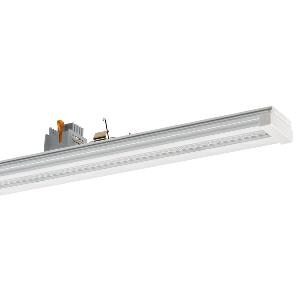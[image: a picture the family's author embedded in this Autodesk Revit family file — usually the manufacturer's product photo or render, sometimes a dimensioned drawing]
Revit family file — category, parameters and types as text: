
# Revit family: conveo_-_cvg_8000_850_xn-l_da_7_226848409-00804979_7b88
name_source: partatom
category: Lighting Fixtures
units: mm (PartAtom-declared; Revit-internal decimal feet)

## family parameters
Cut with Voids When Loaded = No
Host = Face
Light Source = No
Part Type = Normal
Room Calculation Point = No
Round Connector Dimension = Use Diameter
Shared = No

## types (1)
- CONVEO - CVG 8000/850/xN-L/DA/7 (1 x LED, 8450 lm, 5000K)
    Apparent Load = 51 VA
    Approval mark = CE
    CIE Flux Codes = 84 95 99 100 100
    Color Rendering = 80-89
    Color Temperature = 5000K
    Control Gear = Electronic ballast
    Default Elevation = 1800 mm
    Description = CVG 8000/850/xN-L/DA/7|Continuous-row system|light source: LED|work equipment: Adjustable electronic ballast, digital DALI|connected load: 220-240 V, 50-60 Hz|Power consumption: approx. 51 W|luminous flux: 8450 lm|luminous efficacy: 165 lm/W|colour temperature: Cold white, ca. 5000 K|color rendering index (CRI): >= 80|chromaticity tolerance:  3 SDCM|System of protection: IP 54|class of protection: I|technology: Continuously dimmable|luminaire body|material: Aluminium|surface: Powder coatet|colour: White|lamp cover: Acrylic (PMMA), Satine|weight (net): approx. 1.9 kg|Fastening: Available separately|maximum ambient temperature: 42 ░C|glare control: Lens optics|Approval mark: VDE - ENEC|
    Frequency = 50 Hz
    Height = 70 mm
    Lamp = 1 x LED
    Lamp Light Flux = 8450 lm
    Lamp count = 1
    Length = 1500 mm
    Luminous efficacy = 166 lm/W
    Manufacturer = Waldmann
    ModVariant = No
    Model = 226848409-00804979
    Mounting Place = Ceiling
    Mounting Type = Pendant
    Number of Poles = 1
    OnlyDefault = Yes
    Power Factor = 1
    Product Name = CONVEO - CVG 8000/850/xN-L/DA/7
    Product group = Continuous-row system (industry)
    ProductGroupID = 301
    Protection Class = Protection class I
    Protection Degree = IP 54
    RLX_Detail_Level = 1
    RlxData = <blob elided: 101013 chars, md5=59f7ad95>
    Socket = socket
    Standby Power = 0 W
    System Light Flux = 8450 lm
    System Power = 51 W
    Type Comments = Product without accessories
    Type Image = 226848259-00804964_1l7.jpg
    URL = http://relux.com
    VarID = ---
    Voltage = 230 V
    Voltage Range = 220-240 V
    Weight = 0.00 kg
    Width = 64 mm

## geometry (parser evidence)
native form markers: Blend x4, Sweep x10
no freeform markers — native parametric forms only
